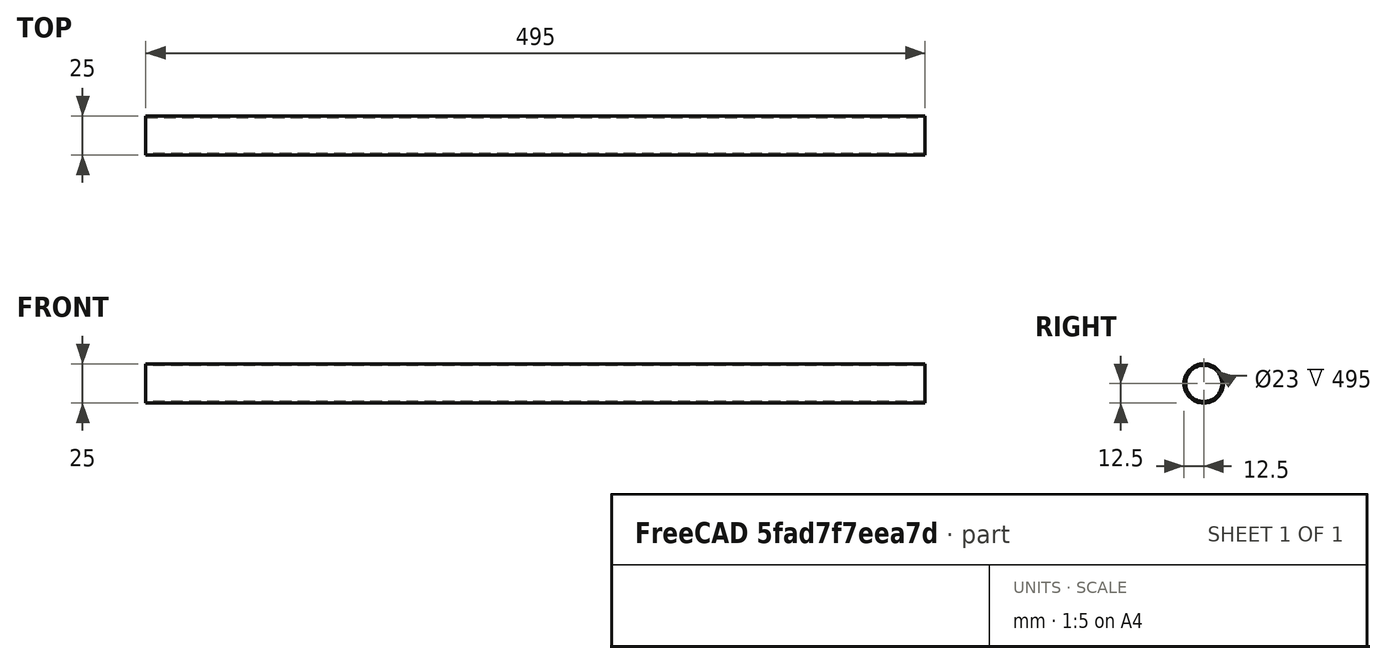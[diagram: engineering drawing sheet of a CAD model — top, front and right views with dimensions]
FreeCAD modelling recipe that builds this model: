
FCSTD DOCUMENT  (FreeCAD 0.21R33771 (Git))
Label: wellhofer-drive-shaft-cover
License: All rights reserved
LicenseURL: https://en.wikipedia.org/wiki/All_rights_reserved
objects: Sketcher::SketchObject×1, PartDesign::Pad×1, PartDesign::Body×1
note: 4 computed .brp shape members not serialized (recipe doc carries the construction recipe); baked Part::Feature solids carry a one-line shape summary decoded from their .brp

FEATURE [Sketcher::SketchObject] Sketch
  FullyConstrained = true
  MapMode = 5
  Placement = pos=(0,0,0) rot=(0.57735,0.57735,0.57735;2.0944rad)
  Support = -> [YZ_Plane]
  sketch-geometry (2):
    g0: Circle CenterX=0 CenterY=0 CenterZ=0 NormalX=0 NormalY=0 NormalZ=1 AngleXU=0 Radius=12.5
    g1: Circle CenterX=0 CenterY=0 CenterZ=0 NormalX=0 NormalY=0 NormalZ=1 AngleXU=0 Radius=11.5
  constraints (4):
    c: Coincident(g0,g-1)
    c: Coincident(g1,g0)
    c: Diameter(g1) = 23
    c: Diameter(g0) = 25
FEATURE [PartDesign::Pad] Pad
  Direction = (1,-2e-16,3e-16)
  Length = 495
  Length2 = 10
  Placement = pos=(0,0,0) rot=(1,1,1;2.0944rad)
  Profile = -> Sketch
  ReferenceAxis = -> Sketch [N_Axis]
  Type = 0
FEATURE [PartDesign::Body] Body
  Group = -> [Sketch,Pad]
  Origin = -> Origin
  Tip = -> Pad
